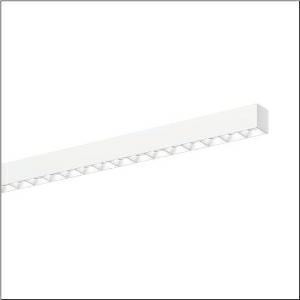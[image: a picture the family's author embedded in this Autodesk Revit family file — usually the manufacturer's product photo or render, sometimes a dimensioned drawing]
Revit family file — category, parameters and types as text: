
# Revit family: silica_21_51mx26dc4awb
name_source: partatom
category: Lighting Fixtures
units: mm (PartAtom-declared; Revit-internal decimal feet)

## family parameters
Cut with Voids When Loaded = No
Host = Face
Light Source = No
Part Type = Normal
Room Calculation Point = No
Round Connector Dimension = Use Diameter
Shared = No

## types (1)
- --- (1 x LED, 10800 lm, 60.6 W, 4000K)
    Apparent Load = 61 VA
    CIE Flux Codes = 83 98 100 100 100
    Color Rendering = 80
    Color Temperature = 4000K
    Default Elevation = 1800 mm
    Description = Silica 21, office luminaire, primary light control with darklight reflector, of PMMA, white, CAT 2 (L<= 3000cd/m²), light emission: direct distribution, primary light characteristic: symmetric, installation type: surface-mounted, LED, rated luminous flux: 10.800lm, luminous efficacy: 178lm/W, light colour: 840, colour temperature: 4000K, control gear: DALI 2, with terminal, 3+2-pole, max. 2.5mm², mains connection: 220..240V, AC, 50/60Hz, rated input power: 60.6W, luminaire housing, of aluminium, traffic white (RAL 9016), length: 3.004mm, width: 53mm, height: 53mm, protection rating (complete): IP20, insulation class (complete): insulation class I (protective earthing), certification: CE, permissible operating ambient temperature: 0..+35°C, standard: EN 50419, packaging unit: 1 piece
    Height = 53 mm
    Lamp = 1 x LED
    Lamp Light Flux = 10800 lm
    Lamp Power = 60.6 W
    Lamp count = 1
    Length = 3004 mm
    Luminous efficacy = 178 lm/W
    Manufacturer = Siteco
    ModVariant = No
    Model = 51MX26DC4AWB
    Mounting Place = Ceiling
    Mounting Type = Surface mounted
    Number of Poles = 1
    OnlyDefault = Yes
    Power Factor = 1
    Product Name = Silica 21
    Product group = office luminaire | ceiling mounted
    ProductGroupID = 301
    Protection Class = Protection class I
    Protection Degree = IP 20
    RLX_Detail_Level = 1
    RLX_Emergency_Light_Flux = 0 lm
    RLX_Emergency_Type = 0
    RLX_Emergency_Type_DB = No
    RlxData = <blob elided: 58813 chars, md5=e2e438a0>
    Socket = socket
    Standby Power = 0 W
    System Light Flux = 10800 lm
    System Power = 61 W
    Type Comments = factory setting: luminous flux: 100 % | dim-lin: 254 | 336 mA
    Type Image = l_1335934.jpg
    URL = http://relux.com
    VarID = @adj_124377
    Voltage = 0 V
    Weight = 0.00 kg
    Width = 53 mm

## geometry (parser evidence)
native form markers: Blend x4, Sweep x10
no freeform markers — native parametric forms only
